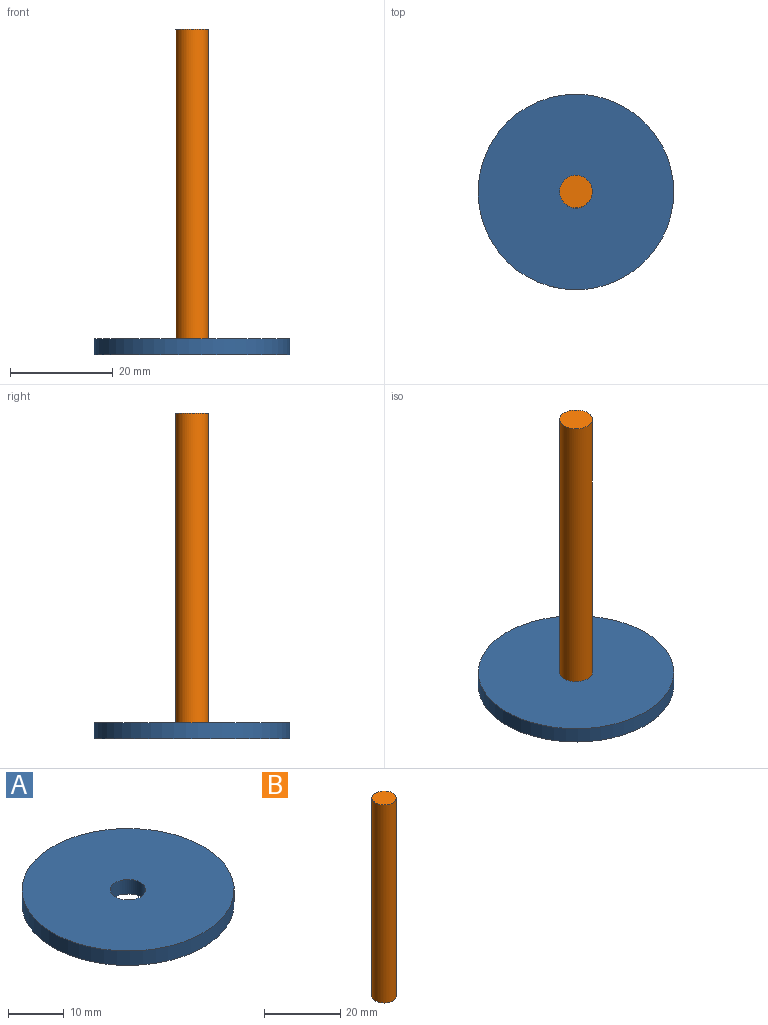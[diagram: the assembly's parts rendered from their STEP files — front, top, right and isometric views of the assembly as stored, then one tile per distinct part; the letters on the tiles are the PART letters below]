
ASSEMBLY  parts=2 mates=1
PART A: 4 faces, bbox 38.1x38.1x3.2 mm
  f0: cylinder r=3.17mm len=6.35mm, axis (0,0,-1), area 63.3mm2, adj f2,f3
  f1: cylinder r=19.05mm len=38.1mm, axis (0,0,-1), area 380mm2, adj f2,f3
  f2: plane 38.1x38.1mm, normal (0,0,1), area 1108.4mm2, adj f0,f1
  f3: plane 38.1x38.1mm, normal (0,0,-1), area 1108.4mm2, adj f0,f1
PART B: 3 faces, bbox 6.4x6.4x63.5 mm
  f0: plane 6.35x6.35mm, normal (0,0,1), area 31.7mm2, adj f1
  f1: cylinder r=3.17mm len=63.5mm, axis (0,0,-1), area 1266.8mm2, adj f0,f2
  f2: plane 6.35x6.35mm, normal (0,0,-1), area 31.7mm2, adj f1
PLACE A t=(69.85,0,-69.85)mm
PLACE B t=(69.85,0,-69.85)mm
MATE fastened B.f1 <-> A.f1  axis (0,0,-1) through (0,0,0)mm
